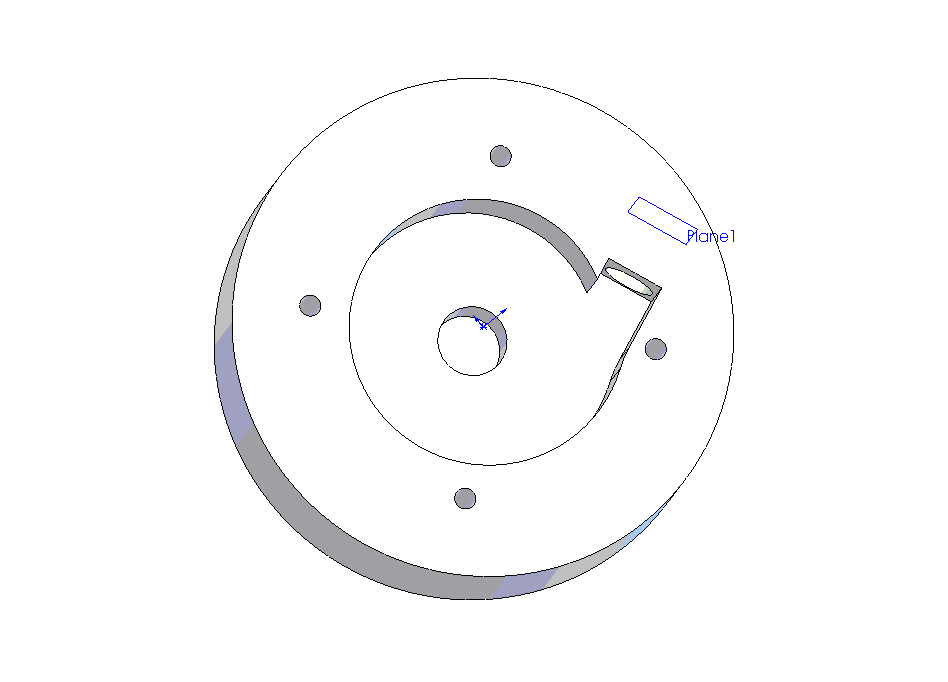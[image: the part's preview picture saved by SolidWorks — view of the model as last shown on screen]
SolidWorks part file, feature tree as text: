
SOLIDWORKS PART (.sldprt)
format: sldprt  version: not decoded by parser v0  size: 273,920 bytes
history: native  units: mm
features: sketch x7, cut_extrude x4, extrude x2, material x1, helix x1, fillet x1, plane x1 (+13 scaffold rows collapsed)
feature tree (30):
  scaffold x13  (default folders/planes/origin — collapsed)
  material  "Material <not specified>"
  sketch  "Sketch1"  dims[D1=0.0mm]
  helix  "Helix/Spiral1"  Pitch=5mm
  sketch  "Sketch3"  dims[c1.D3=~36.070819mm c1.D2=50.0mm c1.D4=50.0mm c2.D3=50.0mm c2.D2=10.0mm c3.D3=30.0mm c3.D7=130.0mm c3.D2=18.0mm c4.D3=~15.208157mm c4.D4=25.0mm c4.D5=~13.687265mm c5.D3=15.0mm c5.D2=15.6mm c5.D4=21.6mm c5.D5=3.0mm c5.D6=~3.673503mm c6.D4=30.0mm c6.D6=~3.380416mm c7.D4=3.0mm c7.D6=~28.014445mm c8.D4=28.0mm c8.D6=~16.897538mm c8.D1=0.0mm c8.D2=15.0mm c9.D1=0.0mm c9.D4=10.0mm c10.D1=0.0mm c10.D5=3.0mm c10.D6=3.0mm]
  extrude  "Extrude1"  Depth=34mm
  cut_extrude  "Cut-Extrude2"  [1 undecoded]
  sketch  "Sketch3<6>"  dims[D1=20.0mm]
  extrude  "Extrude6"  [1 undecoded]
  sketch  "Sketch3<7>"
  sketch  "Sketch22"  dims[D1=13.6mm D2=8.0mm]
  cut_extrude  "Cut-Extrude3"  Depth=3mm
  fillet  "Fillet1"  Radius=3mm
  sketch  "Sketch26"  dims[D1=18.0mm]
  cut_extrude  "Cut-Extrude4"  [1 undecoded]
  plane  "Plane1"  Offset=17.8mm
  sketch  "Sketch27"  dims[D1=18.0mm]
  cut_extrude  "Cut-Extrude5"  [1 undecoded]
decode coverage: 10 of 15 modeling features carry decoded parameters
note: ~ marks probable driven/reference dimensions
note: 4 parameter values undecoded
summary: no parameter record found for 4 features
note: suppression state not decoded; provenance and decode notes live in map.json
